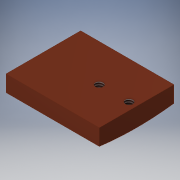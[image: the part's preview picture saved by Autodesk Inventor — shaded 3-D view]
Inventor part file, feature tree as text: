
AUTODESK INVENTOR PART (.ipt)
format: ipt  version: 2018 (Build 220112000, 112)  size: 127,488 bytes
history: native  units: in
note: dims shown in document units (in); Inventor stores cm internally (conversion verified against a paired STEP export)
features: sketch x4, extrude x2, hole x2
ambient origin geometry x8: Origin, YZ Plane, XZ Plane, XY Plane, X Axis, Y Axis, Z Axis, Center Point
bodies: Solid1 (feature_tree)
feature tree (8):
  extrude  "Extrusion1"  Depth=1.0in
  hole  "Hole1"  [1 undecoded]
  extrude  "Extrusion2"  Depth=3.875in
  hole  "Hole2"  [1 undecoded]
  sketch  "Sketch1"  dims[d0=1.25in d1=1.0in]
  sketch  "Sketch2"  dims[d2=0.25in d3=0.0in d4=0.25in]
  sketch  "Sketch3"  dims[d5=180.0deg]
  sketch  "Sketch4"  dims[d6=0.104in d7=0.276in d8=0.375in d9=0.25in d10=0.5635in d11=0.75in d12=0.8108in d14=3.875in d15=90.0deg d16=7.75in d17=0.25in d18=0.0in d19=0.75in d20=0.0in d21=0.4in d22=0.0in d23=0.104in d24=0.276in d25=0.375in d26=0.25in d27=0.5635in d28=0.75in d29=0.8108in]
note: 2 required parameter values undecoded (feature->parameter linkage not recoverable at this tier; creation-order binding heuristic only, values carry confidence <= 0.55)
